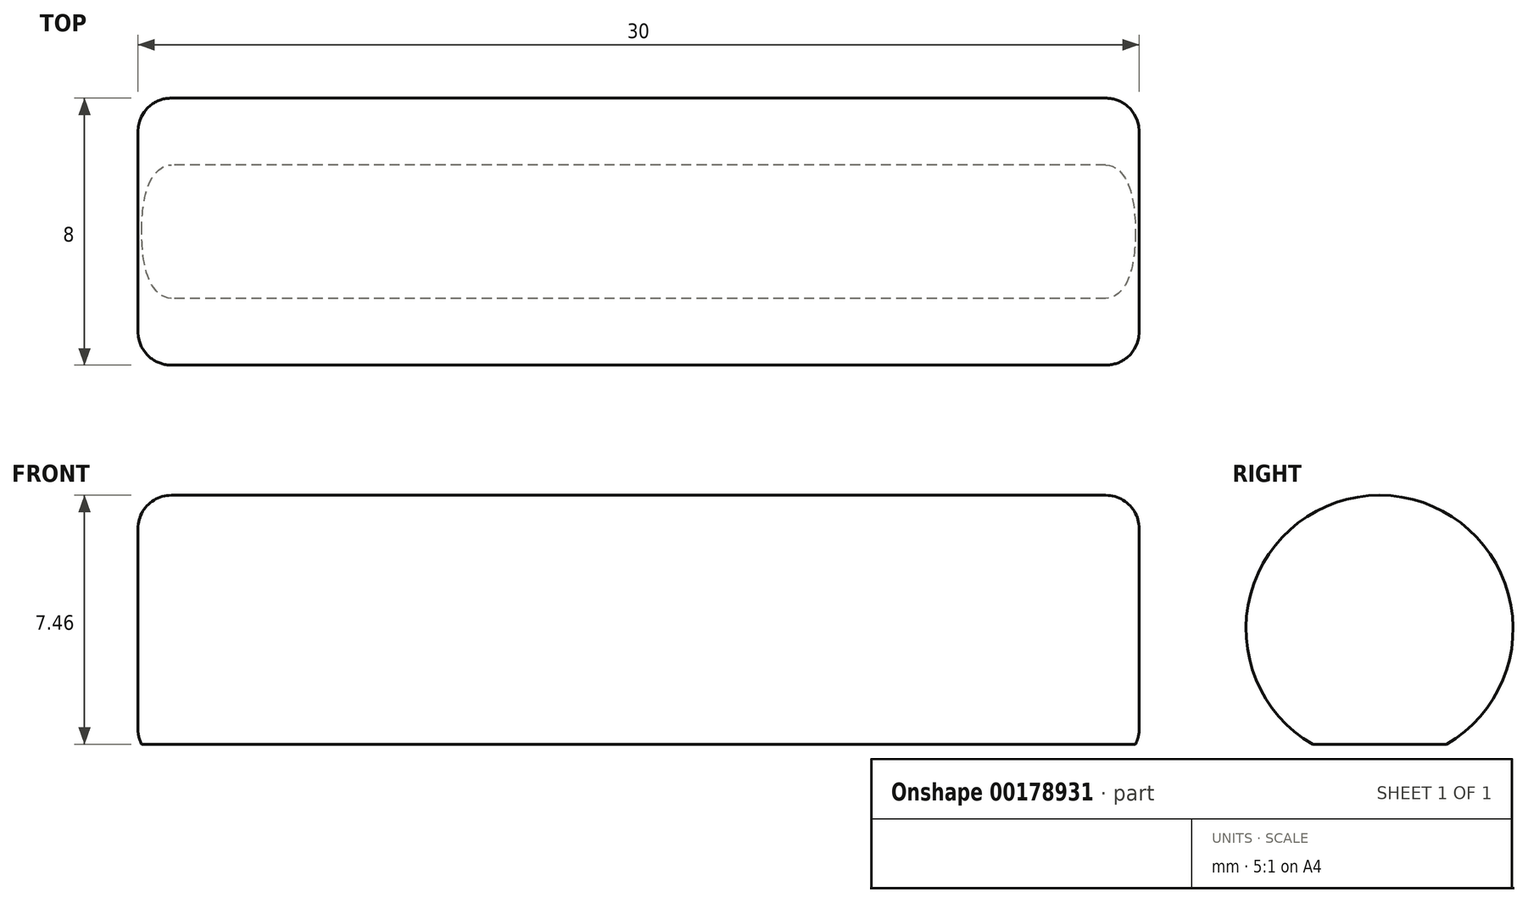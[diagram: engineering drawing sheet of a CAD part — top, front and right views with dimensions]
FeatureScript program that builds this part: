
annotation { "Feature Type Name" : "Feature", "Feature Type Description" : "" }
export const myFeature = defineFeature(function(context is Context, id is Id, definition is map)
    precondition{}
    {
        {
            var Q0;
            Q0=qCreatedBy(makeId("Right.planeOp"),FACE);
            var sketch = newSketch(context, id + "F0", { "sketchPlane" : qUnion([Q0])});
            skCircle(sketch, "E0", {"center": v(0, 0) * mm, "radius": 4 * mm});
            skLineSegment(sketch, "E1", {"start": v(-2, -3.46) * mm, "end": v(2, -3.46) * mm});
            skSolve(sketch);
        }
        {
            var Q0;
            {var subQ0=sQuery(id+"F0.wireOp",EDGE,"E1");Q0=makeQuery(id+"F0.imprint","IMPRINT",FACE,{"disambiguationData":[TD([[makeQuery(id+"F0.imprint","IMPRINT",EDGE,{"derivedFrom":subQ0}),1.0]])]});}
            extrude(context, id + "F1", {"entities" : qUnion([Q0]), "depth" : 30 * mm});
        }
        {
            var Q0;
            Q0=makeQuery(id+"F1.opExtrude","CAP_EDGE",EDGE,{"disambiguationData":[OSD([sQuery(id+"F0.wireOp",EDGE,"E0")])],"isStart":false});
            var Q1;
            Q1=makeQuery(id+"F1.opExtrude","CAP_EDGE",EDGE,{"disambiguationData":[OSD([sQuery(id+"F0.wireOp",EDGE,"E0")])],"isStart":true});
            fillet(context, id + "F2", {"entities" : qUnion([Q0, Q1]), "radius" : 1 * mm, "tangentPropagation" : true, "allowEdgeOverflow" : false});
        }
    });
